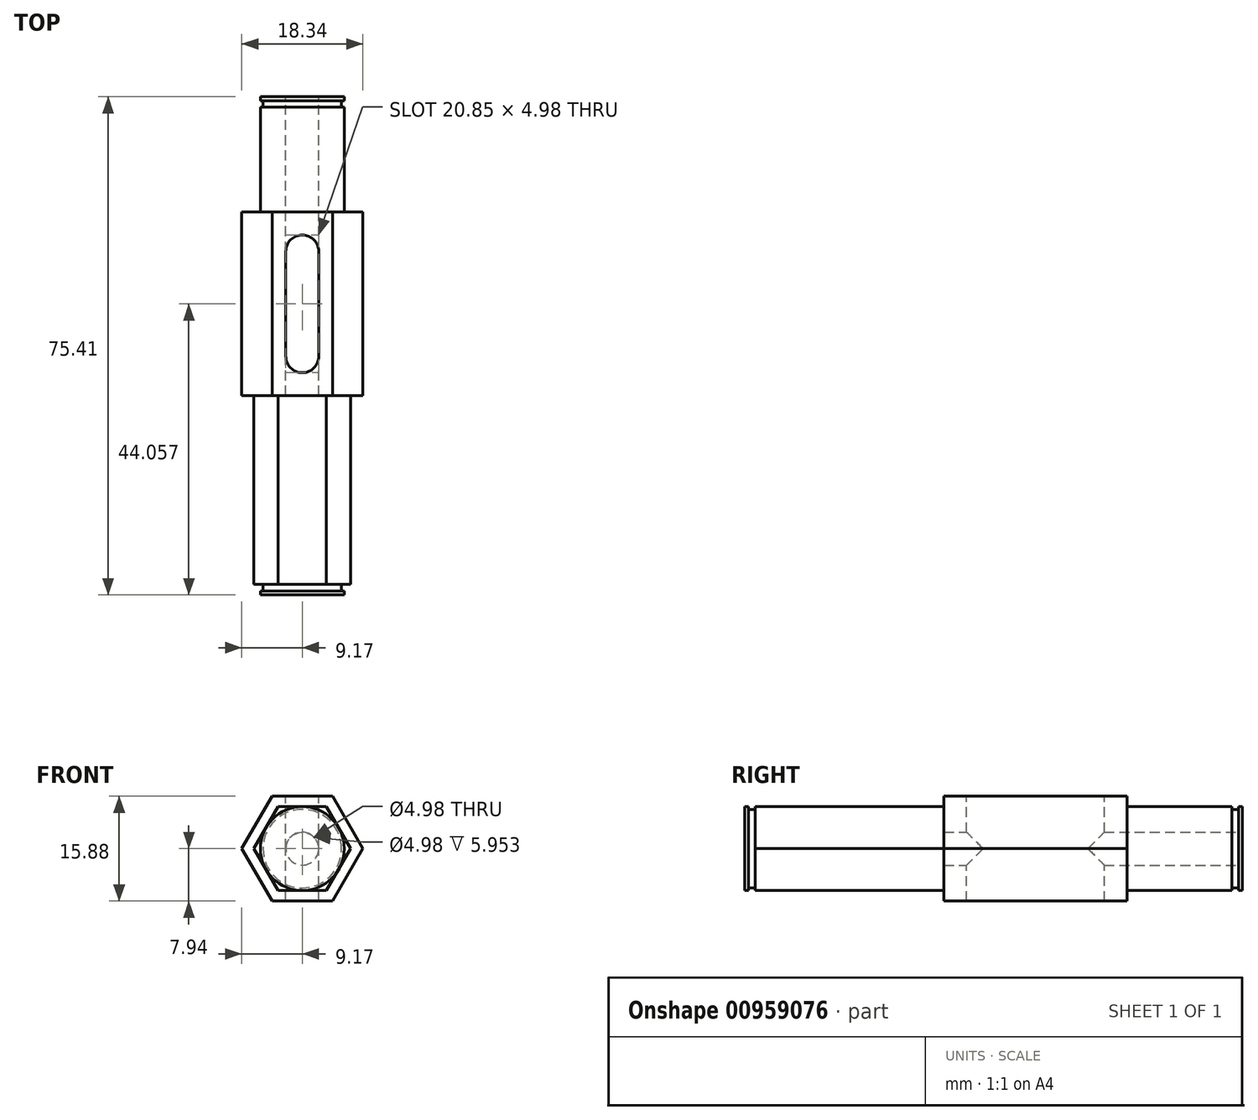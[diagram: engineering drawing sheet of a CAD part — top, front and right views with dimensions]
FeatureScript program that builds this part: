
annotation { "Feature Type Name" : "Feature", "Feature Type Description" : "" }
export const myFeature = defineFeature(function(context is Context, id is Id, definition is map)
    precondition{}
    {
        {
            var Q0;
            Q0=qCreatedBy(makeId("Front.planeOp"),FACE);
            var sketch = newSketch(context, id + "F0", { "sketchPlane" : qUnion([Q0])});
            skCircle(sketch, "E0", {"center": v(0, 0) * mm, "radius": 6.35 * mm});
            skCircle(sketch, "E1", {"center": v(0, 0) * mm, "radius": 2.49 * mm});
            skSolve(sketch);
        }
        {
            var Q0;
            Q0 = qSketchRegion(id + "F0", true);
            extrude(context, id + "F1", {"entities" : qUnion([Q0]), "depth" : 17.46 * mm, "offsetDistance" : 25.4 * mm});
        }
        {
            var Q0;
            Q0=makeQuery(id+"F1.opExtrude","CAP_FACE",FACE,{"disambiguationData":[OSD([sQuery(id+"F0.wireOp",EDGE,"E0"),sQuery(id+"F0.wireOp",EDGE,"E1")])],"isStart":false});
            var sketch = newSketch(context, id + "F2", { "sketchPlane" : qUnion([Q0])});
            skCircle(sketch, "E2.cCircle", {"center": v(0, 0) * mm, "radius": 7.94 * mm, "construction": true});
            skLineSegment(sketch, "E2.0", {"start": v(-4.58, 7.94) * mm, "end": v(4.58, 7.94) * mm});
            skLineSegment(sketch, "E2.1", {"start": v(4.58, 7.94) * mm, "end": v(9.17, 0) * mm});
            skLineSegment(sketch, "E2.2", {"start": v(9.17, 0) * mm, "end": v(4.58, -7.94) * mm});
            skLineSegment(sketch, "E2.3", {"start": v(4.58, -7.94) * mm, "end": v(-4.58, -7.94) * mm});
            skLineSegment(sketch, "E2.4", {"start": v(-4.58, -7.94) * mm, "end": v(-9.17, 0) * mm});
            skLineSegment(sketch, "E2.5", {"start": v(-9.17, 0) * mm, "end": v(-4.58, 7.94) * mm});
            skPoint(sketch, "E2.0.midPoint", {"position": v(0, 7.94) * mm});
            skCircle(sketch, "E3", {"center": v(0, 0) * mm, "radius": 2.49 * mm});
            skSolve(sketch);
        }
        {
            var Q0;
            Q0 = qSketchRegion(id + "F2", true);
            extrude(context, id + "F3", {"entities" : qUnion([Q0]), "operationType" : NewBodyOperationType.ADD, "depth" : 27.78 * mm, "offsetDistance" : 25.4 * mm});
        }
        {
            var Q0;
            Q0=makeQuery(id+"F3.opExtrude","SWEPT_FACE",FACE,{"disambiguationData":[OSD([sQuery(id+"F2.wireOp",EDGE,"E2.0")])]});
            var sketch = newSketch(context, id + "F4", { "sketchPlane" : qUnion([Q0])});
            skLineSegment(sketch, "E4", {"start": v(0, -23.42) * mm, "end": v(0, -39.3) * mm, "construction": true});
            skArc(sketch, "E5.0.startCap", {"start": v(-2.49, -23.42) * mm, "mid": v(0, -20.93) * mm, "end": v(2.49, -23.42) * mm});
            skArc(sketch, "E5.0.endCap", {"start": v(2.49, -39.3) * mm, "mid": v(0, -41.78) * mm, "end": v(-2.49, -39.3) * mm});
            skLineSegment(sketch, "E5.0.left", {"start": v(2.49, -23.42) * mm, "end": v(2.49, -39.3) * mm});
            skLineSegment(sketch, "E5.0.right", {"start": v(-2.49, -23.42) * mm, "end": v(-2.49, -39.3) * mm});
            skPoint(sketch, "E6", {"position": v(0, -17.46) * mm});
            skLineSegment(sketch, "E7", {"start": v(0, -31.35) * mm, "end": v(4.58, -31.35) * mm, "construction": true});
            skSolve(sketch);
        }
        {
            var Q0;
            Q0 = qSketchRegion(id + "F4", true);
            extrude(context, id + "F5", {"entities" : qUnion([Q0]), "operationType" : NewBodyOperationType.REMOVE, "endBound" : BoundingType.THROUGH_ALL, "oppositeDirection" : true, "depth" : 25.4 * mm, "offsetDistance" : 25.4 * mm});
        }
        {
            var Q0;
            Q0=makeQuery(id+"F3.opExtrude","CAP_FACE",FACE,{"disambiguationData":[OSD([sQuery(id+"F2.wireOp",EDGE,"E2.0"),sQuery(id+"F2.wireOp",EDGE,"E2.1"),sQuery(id+"F2.wireOp",EDGE,"E2.2"),sQuery(id+"F2.wireOp",EDGE,"E2.3"),sQuery(id+"F2.wireOp",EDGE,"E2.4"),sQuery(id+"F2.wireOp",EDGE,"E2.5"),sQuery(id+"F2.wireOp",EDGE,"E3")])],"isStart":false});
            var sketch = newSketch(context, id + "F6", { "sketchPlane" : qUnion([Q0])});
            skCircle(sketch, "E8.cCircle", {"center": v(0, 0) * mm, "radius": 6.35 * mm, "construction": true});
            skLineSegment(sketch, "E8.0", {"start": v(3.67, -6.35) * mm, "end": v(-3.67, -6.35) * mm});
            skLineSegment(sketch, "E8.1", {"start": v(-3.67, -6.35) * mm, "end": v(-7.33, 0) * mm});
            skLineSegment(sketch, "E8.2", {"start": v(-7.33, 0) * mm, "end": v(-3.67, 6.35) * mm});
            skLineSegment(sketch, "E8.3", {"start": v(-3.67, 6.35) * mm, "end": v(3.67, 6.35) * mm});
            skLineSegment(sketch, "E8.4", {"start": v(3.67, 6.35) * mm, "end": v(7.33, 0) * mm});
            skLineSegment(sketch, "E8.5", {"start": v(7.33, 0) * mm, "end": v(3.67, -6.35) * mm});
            skPoint(sketch, "E8.0.midPoint", {"position": v(0, -6.35) * mm});
            skSolve(sketch);
        }
        {
            var Q0;
            Q0 = qSketchRegion(id + "F6", true);
            extrude(context, id + "F7", {"entities" : qUnion([Q0]), "operationType" : NewBodyOperationType.ADD, "depth" : 30.16 * mm, "offsetDistance" : 25.4 * mm});
        }
        {
            var Q0;
            Q0=qCreatedBy(makeId("Top.planeOp"),FACE);
            var sketch = newSketch(context, id + "F8", { "sketchPlane" : qUnion([Q0])});
            skLineSegment(sketch, "E9", {"start": v(-6.35, -75.4) * mm, "end": v(-6.35, -74.8) * mm});
            skLineSegment(sketch, "E10", {"start": v(-6.35, -74.8) * mm, "end": v(-5.94, -74.8) * mm});
            skLineSegment(sketch, "E11", {"start": v(-5.94, -74.8) * mm, "end": v(-5.94, -73.82) * mm});
            skLineSegment(sketch, "E12", {"start": v(-5.94, -73.82) * mm, "end": v(-7.33, -73.82) * mm});
            skLineSegment(sketch, "E13", {"start": v(0, -75.4) * mm, "end": v(0, -45.24) * mm, "construction": true});
            skLineSegment(sketch, "E14.MirrorCS", {"start": v(6.35, -75.4) * mm, "end": v(6.35, -74.8) * mm});
            skLineSegment(sketch, "E15.MirrorCS", {"start": v(5.94, -73.82) * mm, "end": v(7.33, -73.82) * mm});
            skLineSegment(sketch, "E16.MirrorCS", {"start": v(5.94, -74.8) * mm, "end": v(5.94, -73.82) * mm});
            skLineSegment(sketch, "E17.MirrorCS", {"start": v(6.35, -74.8) * mm, "end": v(5.94, -74.8) * mm});
            skLineSegment(sketch, "E18", {"start": v(0, -75.4) * mm, "end": v(0, 0) * mm, "construction": true});
            skLineSegment(sketch, "E19", {"start": v(0, -37.7) * mm, "end": v(-9.17, -37.7) * mm, "construction": true});
            skLineSegment(sketch, "E20", {"start": v(-7.33, -73.82) * mm, "end": v(-7.33, -75.4) * mm});
            skLineSegment(sketch, "E21", {"start": v(-7.33, -75.4) * mm, "end": v(-6.35, -75.4) * mm});
            skLineSegment(sketch, "E22", {"start": v(7.33, -73.82) * mm, "end": v(7.33, -75.4) * mm});
            skLineSegment(sketch, "E23", {"start": v(7.33, -75.4) * mm, "end": v(6.35, -75.4) * mm});
            skLineSegment(sketch, "E24.MirrorCS", {"start": v(7.33, 0) * mm, "end": v(6.35, 0) * mm});
            skLineSegment(sketch, "E25.MirrorCS", {"start": v(-6.35, -0.6) * mm, "end": v(-5.94, -0.6) * mm});
            skLineSegment(sketch, "E26.MirrorCS", {"start": v(-5.94, -0.6) * mm, "end": v(-5.94, -1.59) * mm});
            skLineSegment(sketch, "E27.MirrorCS", {"start": v(-7.33, 0) * mm, "end": v(-6.35, 0) * mm});
            skLineSegment(sketch, "E28.MirrorCS", {"start": v(5.94, -0.6) * mm, "end": v(5.94, -1.59) * mm});
            skLineSegment(sketch, "E29.MirrorCS", {"start": v(6.35, -0.6) * mm, "end": v(5.94, -0.6) * mm});
            skLineSegment(sketch, "E30.MirrorCS", {"start": v(-5.94, -1.59) * mm, "end": v(-7.33, -1.59) * mm});
            skLineSegment(sketch, "E31.MirrorCS", {"start": v(6.35, 0) * mm, "end": v(6.35, -0.6) * mm});
            skLineSegment(sketch, "E32.MirrorCS", {"start": v(5.94, -1.59) * mm, "end": v(7.33, -1.59) * mm});
            skLineSegment(sketch, "E33.MirrorCS", {"start": v(-6.35, 0) * mm, "end": v(-6.35, -0.6) * mm});
            skLineSegment(sketch, "E34.MirrorCS", {"start": v(-7.33, -1.59) * mm, "end": v(-7.33, 0) * mm});
            skLineSegment(sketch, "E35.MirrorCS", {"start": v(7.33, -1.59) * mm, "end": v(7.33, 0) * mm});
            skSolve(sketch);
        }
        {
            var Q0;
            Q0 = qSketchRegion(id + "F8", true);
            var Q1;
            Q1=sQuery(id+"F8.wireOp",EDGE,"E18");
            revolve(context, id + "F9", {"operationType" : NewBodyOperationType.REMOVE, "surfaceOperationType" : NewSurfaceOperationType.NEW, "entities" : qUnion([Q0]), "axis" : qUnion([Q1]), "revolveType" : RevolveType.FULL, "oppositeDirection" : true});
        }
    });
